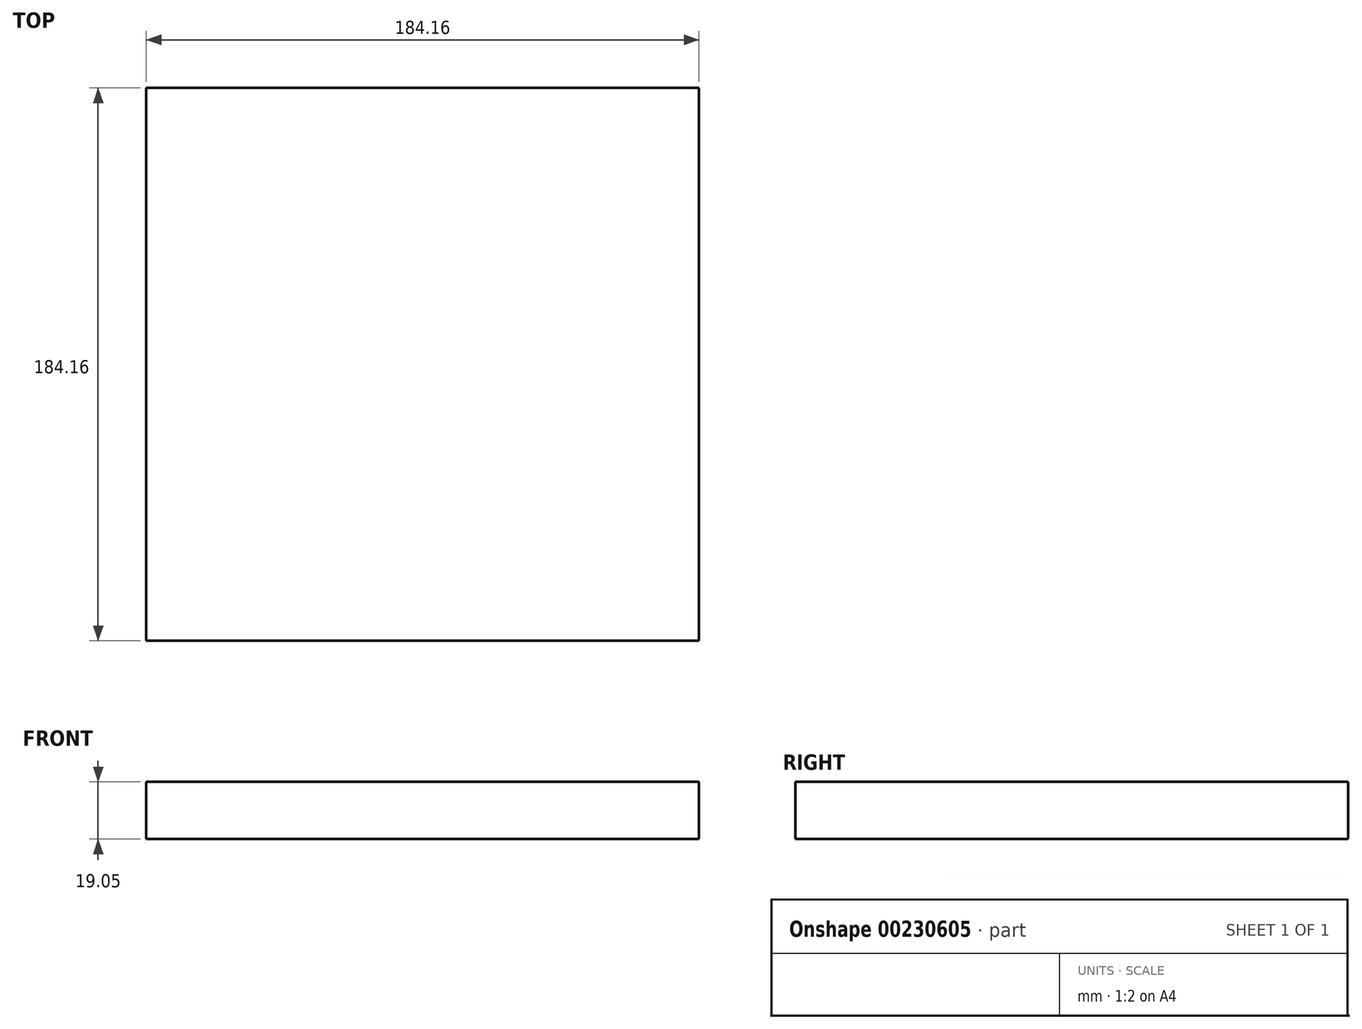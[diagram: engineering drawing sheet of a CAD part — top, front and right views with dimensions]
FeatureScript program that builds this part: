
annotation { "Feature Type Name" : "Feature", "Feature Type Description" : "" }
export const myFeature = defineFeature(function(context is Context, id is Id, definition is map)
    precondition{}
    {
        {
            var Q0;
            Q0=qCreatedBy(makeId("Top.planeOp"),FACE);
            var sketch = newSketch(context, id + "F0", { "sketchPlane" : qUnion([Q0])});
            skLineSegment(sketch, "E0.bottom", {"start": v(-92.07, 92.07) * mm, "end": v(92.08, 92.07) * mm});
            skLineSegment(sketch, "E0.top", {"start": v(-92.08, -92.07) * mm, "end": v(92.08, -92.07) * mm});
            skLineSegment(sketch, "E0.left", {"start": v(-92.07, 92.07) * mm, "end": v(-92.08, -92.07) * mm});
            skLineSegment(sketch, "E0.right", {"start": v(92.08, 92.08) * mm, "end": v(92.08, -92.07) * mm});
            skPoint(sketch, "E0.middle", {"position": v(0, 0) * mm});
            skSolve(sketch);
        }
        {
            var Q0;
            Q0 = qSketchRegion(id + "F0", true);
            extrude(context, id + "F1", {"entities" : qUnion([Q0]), "depth" : 19.05 * mm});
        }
    });
